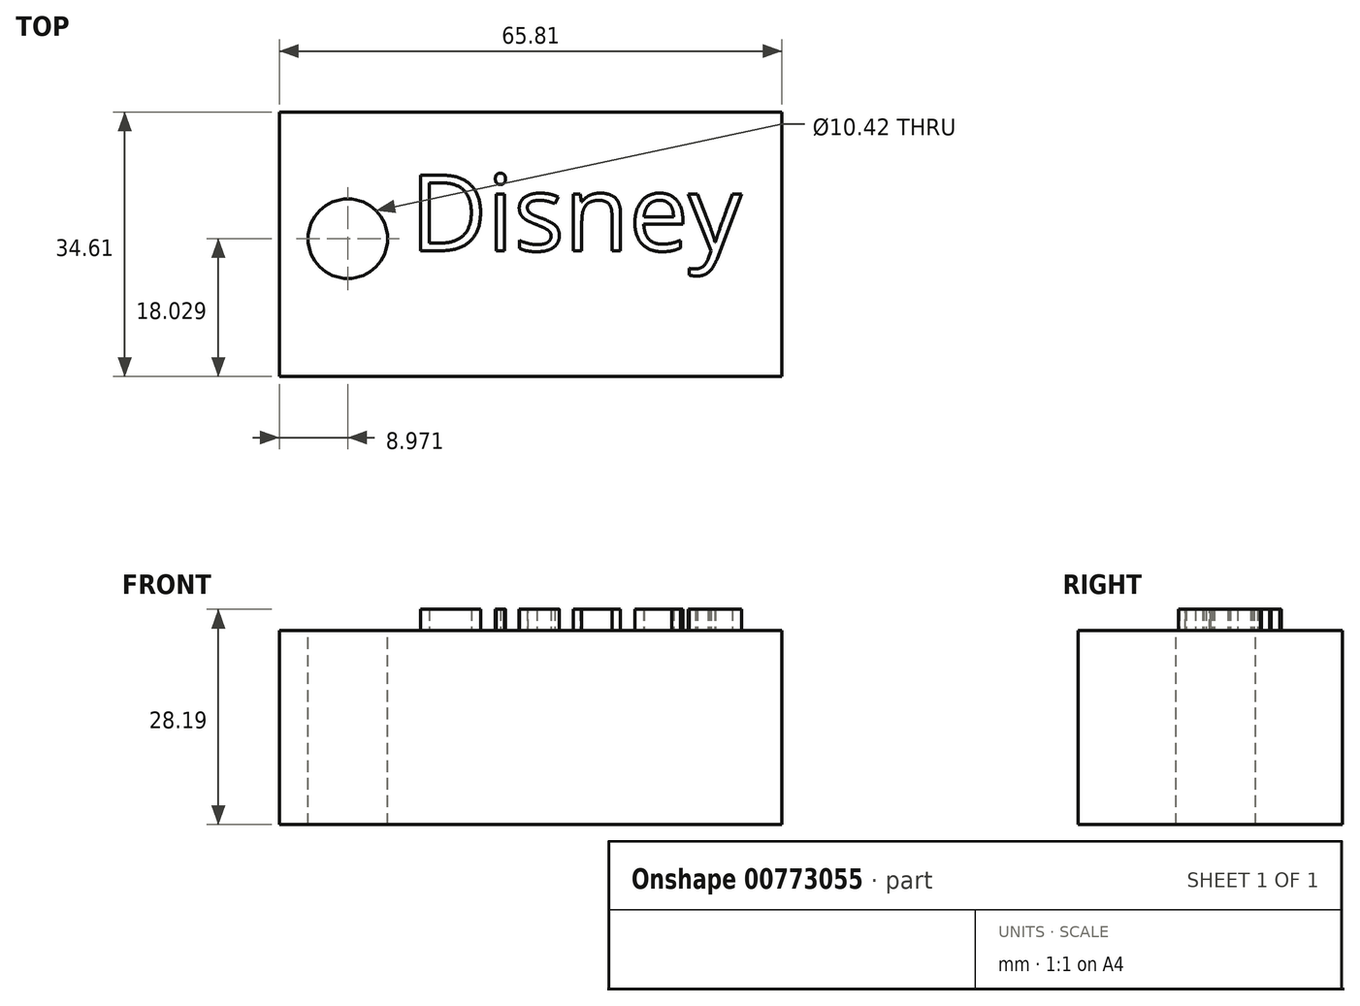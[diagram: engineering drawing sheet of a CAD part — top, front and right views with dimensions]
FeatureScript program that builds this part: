
annotation { "Feature Type Name" : "Feature", "Feature Type Description" : "" }
export const myFeature = defineFeature(function(context is Context, id is Id, definition is map)
    precondition{}
    {
        {
            var Q0;
            Q0=qCreatedBy(makeId("Top.planeOp"),FACE);
            var sketch = newSketch(context, id + "F0", { "sketchPlane" : qUnion([Q0])});
            skLineSegment(sketch, "E0.bottom", {"start": v(6.3, 4.7) * mm, "end": v(-108.21, 4.7) * mm});
            skLineSegment(sketch, "E0.top", {"start": v(6.3, 51.7) * mm, "end": v(-108.21, 51.7) * mm});
            skLineSegment(sketch, "E0.left", {"start": v(6.3, 4.7) * mm, "end": v(6.3, 51.7) * mm});
            skLineSegment(sketch, "E0.right", {"start": v(-108.21, 4.7) * mm, "end": v(-108.21, 51.7) * mm});
            skPoint(sketch, "E0.middle", {"position": v(-50.95, 28.2) * mm});
            skLineSegment(sketch, "E1.bottom", {"start": v(-18.05, 10.9) * mm, "end": v(-83.86, 10.9) * mm});
            skLineSegment(sketch, "E1.top", {"start": v(-18.05, 45.5) * mm, "end": v(-83.86, 45.5) * mm});
            skLineSegment(sketch, "E1.left", {"start": v(-18.05, 10.9) * mm, "end": v(-18.05, 45.5) * mm});
            skLineSegment(sketch, "E1.right", {"start": v(-83.86, 10.9) * mm, "end": v(-83.86, 45.5) * mm});
            skLineSegment(sketch, "E2.bottom", {"start": v(20.4, 7.9) * mm, "end": v(-93.68, 7.9) * mm});
            skLineSegment(sketch, "E2.top", {"start": v(20.4, 79.26) * mm, "end": v(-93.68, 79.26) * mm});
            skLineSegment(sketch, "E2.left", {"start": v(20.4, 7.9) * mm, "end": v(20.4, 79.26) * mm});
            skLineSegment(sketch, "E2.right", {"start": v(-93.68, 7.9) * mm, "end": v(-93.68, 79.26) * mm});
            skPoint(sketch, "E2.middle", {"position": v(-36.64, 43.58) * mm});
            skSolve(sketch);
        }
        {
            var Q0;
            Q0=makeQuery(id+"F0.imprint","IMPRINT",FACE,{"disambiguationData":[TD([[makeQuery(id+"F0.imprint","IMPRINT",EDGE,{"derivedFrom":sQuery(id+"F0.wireOp",EDGE,"E1.bottom")}),-1.0]])]});
            extrude(context, id + "F1", {"entities" : qUnion([Q0]), "depth" : 25.4 * mm, "offsetDistance" : 25.4 * mm});
        }
        {
            var Q0;
            Q0=makeQuery(id+"F1.opExtrude","CAP_FACE",FACE,{"disambiguationData":[OSD([sQuery(id+"F0.wireOp",EDGE,"E1.bottom"),sQuery(id+"F0.wireOp",EDGE,"E1.top"),sQuery(id+"F0.wireOp",EDGE,"E1.left"),sQuery(id+"F0.wireOp",EDGE,"E1.right")])],"isStart":false});
            var sketch = newSketch(context, id + "F2", { "sketchPlane" : qUnion([Q0])});
            skCircle(sketch, "E3", {"center": v(-74.89, 28.93) * mm, "radius": 5.21 * mm});
            skSolve(sketch);
        }
        {
            var Q0;
            Q0 = qSketchRegion(id + "F2", true);
            extrude(context, id + "F3", {"entities" : qUnion([Q0]), "operationType" : NewBodyOperationType.REMOVE, "oppositeDirection" : true, "depth" : 25.4 * mm, "offsetDistance" : 25.4 * mm});
        }
        {
            var Q0;
            Q0=makeQuery(id+"F1.opExtrude","CAP_FACE",FACE,{"disambiguationData":[OSD([sQuery(id+"F0.wireOp",EDGE,"E1.bottom"),sQuery(id+"F0.wireOp",EDGE,"E1.top"),sQuery(id+"F0.wireOp",EDGE,"E1.left"),sQuery(id+"F0.wireOp",EDGE,"E1.right")])],"isStart":false});
            var sketch = newSketch(context, id + "F4", { "sketchPlane" : qUnion([Q0])});
            skText(sketch, "E4", { "text": "Disney\n", "fontName": "OpenSans-Regular.ttf"});
            skPoint(sketch, "E5", {"position": v(-18.05, 28.2) * mm});
            const initialGuessF4  = {"E4": [-0.06675, 0.02736, 1, 0, 0.00996]};
            skSetInitialGuess(sketch, initialGuessF4);
            skSolve(sketch);
        }
        {
            var Q0;
            Q0 = qSketchRegion(id + "F4", true);
            extrude(context, id + "F5", {"entities" : qUnion([Q0]), "operationType" : NewBodyOperationType.ADD, "depth" : 2.8 * mm, "offsetDistance" : 25.4 * mm});
        }
    });
